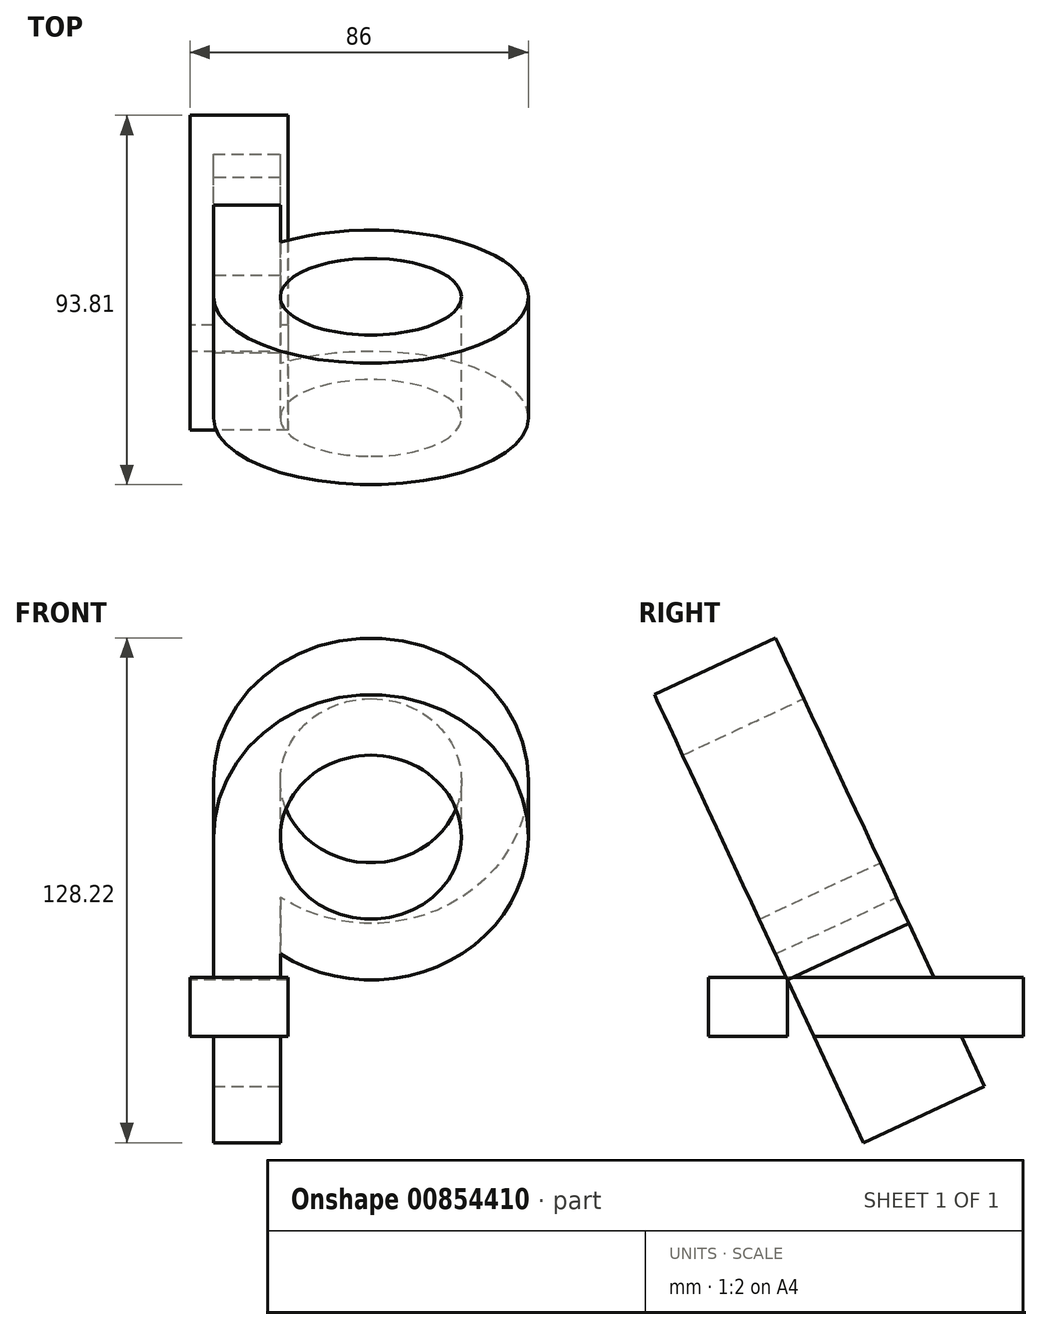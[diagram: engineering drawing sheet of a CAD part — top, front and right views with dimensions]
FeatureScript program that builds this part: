
annotation { "Feature Type Name" : "Feature", "Feature Type Description" : "" }
export const myFeature = defineFeature(function(context is Context, id is Id, definition is map)
    precondition{}
    {
        {
            var Q0;
            Q0=qCreatedBy(makeId("Top.planeOp"),FACE);
            var sketch = newSketch(context, id + "F0", { "sketchPlane" : qUnion([Q0])});
            skLineSegment(sketch, "E0", {"start": v(-43.75, 0) * mm, "end": v(54.87, 0) * mm});
            skSolve(sketch);
        }
        {
            var Q0;
            Q0=sQuery(id+"F0.wireOp",EDGE,"E0");
            cPlane(context, id + "F1", {"entities" : qUnion([Q0]), "cplaneType" : CPlaneType.LINE_ANGLE, "offset" : 25 * mm, "angle" : 25 * degree, "width" : 150 * mm, "height" : 150 * mm});
        }
        {
            var Q0;
            Q0=qCreatedBy(id+"F1.planeOp",FACE);
            var sketch = newSketch(context, id + "F2", { "sketchPlane" : qUnion([Q0])});
            skCircle(sketch, "E1", {"center": v(0, 0) * mm, "radius": 23 * mm});
            skCircle(sketch, "E2", {"center": v(0, 0) * mm, "radius": 40 * mm});
            skSolve(sketch);
        }
        {
            var Q0;
            Q0=qCreatedBy(makeId("Right.planeOp"),FACE);
            var sketch = newSketch(context, id + "F3", { "sketchPlane" : qUnion([Q0])});
            skLineSegment(sketch, "E3.0", {"start": v(-16.9, 36.25) * mm, "end": v(16.9, -36.25) * mm});
            skPoint(sketch, "E4.0", {"position": v(0, 0) * mm});
            skLineSegment(sketch, "E5", {"start": v(-36.47, -65) * mm, "end": v(44.94, -65) * mm});
            skSolve(sketch);
        }
        {
            var Q0;
            Q0=makeQuery(id+"F2.imprint","IMPRINT",FACE,{"disambiguationData":[TD([[makeQuery(id+"F2.imprint","IMPRINT",EDGE,{"derivedFrom":sQuery(id+"F2.wireOp",EDGE,"E1")}),-1.0]])]});
            extrude(context, id + "F4", {"entities" : qUnion([Q0]), "oppositeDirection" : true, "depth" : 34 * mm, "offsetDistance" : 25 * mm});
        }
        {
            var Q0;
            Q0=qCreatedBy(makeId("Right.planeOp"),FACE);
            var sketch = newSketch(context, id + "F5", { "sketchPlane" : qUnion([Q0])});
            skLineSegment(sketch, "E6.0", {"start": v(-47.72, 21.88) * mm, "end": v(-13.9, -50.62) * mm});
            skLineSegment(sketch, "E7", {"start": v(-13.9, -50.62) * mm, "end": v(-3.88, -72.13) * mm});
            skLineSegment(sketch, "E8.0", {"start": v(-16.9, 36.25) * mm, "end": v(16.9, -36.25) * mm});
            skLineSegment(sketch, "E9", {"start": v(16.9, -36.25) * mm, "end": v(33.41, -71.65) * mm});
            skLineSegment(sketch, "E10.0", {"start": v(-36.47, -50) * mm, "end": v(49.3, -50) * mm});
            skLineSegment(sketch, "E11", {"start": v(-13.9, -50.62) * mm, "end": v(-13.9, -68.72) * mm});
            skLineSegment(sketch, "E12.0", {"start": v(-36.47, -65) * mm, "end": v(44.94, -65) * mm});
            skLineSegment(sketch, "E13", {"start": v(-13.9, -65) * mm, "end": v(-33.9, -65) * mm});
            skLineSegment(sketch, "E14", {"start": v(-13.9, -65) * mm, "end": v(46.1, -65) * mm});
            skLineSegment(sketch, "E15", {"start": v(-33.9, -65) * mm, "end": v(-33.9, -50) * mm});
            skLineSegment(sketch, "E16", {"start": v(46.1, -65) * mm, "end": v(46.1, -50) * mm});
            skSolve(sketch);
        }
        {
            var Q0;
            Q0=qCreatedBy(makeId("Right.planeOp"),FACE);
            cPlane(context, id + "F6", {"entities" : qUnion([Q0]), "cplaneType" : CPlaneType.OFFSET, "offset" : 46 * mm, "oppositeDirection" : true, "width" : 150 * mm, "height" : 150 * mm});
        }
        {
            var Q0;
            Q0=qCreatedBy(id+"F6.planeOp",FACE);
            var sketch = newSketch(context, id + "F7", { "sketchPlane" : qUnion([Q0])});
            skLineSegment(sketch, "E17.0.0", {"start": v(-33.9, -50) * mm, "end": v(-33.9, -65) * mm});
            skLineSegment(sketch, "E17.0.1", {"start": v(-33.9, -65) * mm, "end": v(-13.9, -65) * mm});
            skLineSegment(sketch, "E17.0.2", {"start": v(-13.9, -65) * mm, "end": v(-13.9, -50.62) * mm});
            skLineSegment(sketch, "E17.0.3", {"start": v(-13.9, -50.62) * mm, "end": v(-14.2, -50) * mm});
            skLineSegment(sketch, "E17.0.4", {"start": v(-14.2, -50) * mm, "end": v(-33.9, -50) * mm});
            skLineSegment(sketch, "E18.0.0", {"start": v(-7.2, -65) * mm, "end": v(-13.9, -50.62) * mm});
            skLineSegment(sketch, "E18.0.1", {"start": v(-13.9, -50.62) * mm, "end": v(-13.9, -65) * mm});
            skLineSegment(sketch, "E18.0.2", {"start": v(-13.9, -65) * mm, "end": v(-7.2, -65) * mm});
            skLineSegment(sketch, "E19.0.0", {"start": v(23.32, -50) * mm, "end": v(-14.2, -50) * mm});
            skLineSegment(sketch, "E19.0.1", {"start": v(-14.2, -50) * mm, "end": v(-13.9, -50.62) * mm});
            skLineSegment(sketch, "E19.0.2", {"start": v(-13.9, -50.62) * mm, "end": v(-7.2, -65) * mm});
            skLineSegment(sketch, "E19.0.3", {"start": v(-7.2, -65) * mm, "end": v(30.3, -65) * mm});
            skLineSegment(sketch, "E19.0.4", {"start": v(30.3, -65) * mm, "end": v(23.32, -50) * mm});
            skLineSegment(sketch, "E20.0.0", {"start": v(46.1, -50) * mm, "end": v(23.32, -50) * mm});
            skLineSegment(sketch, "E20.0.1", {"start": v(23.32, -50) * mm, "end": v(30.3, -65) * mm});
            skLineSegment(sketch, "E20.0.2", {"start": v(30.3, -65) * mm, "end": v(46.1, -65) * mm});
            skLineSegment(sketch, "E20.0.3", {"start": v(46.1, -65) * mm, "end": v(46.1, -50) * mm});
            skSolve(sketch);
        }
        {
            var Q0;
            Q0=makeQuery(id+"F7.imprint","IMPRINT",FACE,{"disambiguationData":[TD([[makeQuery(id+"F7.imprint","IMPRINT",EDGE,{"derivedFrom":sQuery(id+"F7.wireOp",EDGE,"E17.0.0")}),1.0]])]});
            var Q1;
            Q1=makeQuery(id+"F7.imprint","IMPRINT",FACE,{"disambiguationData":[TD([[makeQuery(id+"F7.imprint","IMPRINT",EDGE,{"derivedFrom":sQuery(id+"F7.wireOp",EDGE,"E18.0.1")}),1.0]])]});
            var Q2;
            Q2=makeQuery(id+"F7.imprint","IMPRINT",FACE,{"disambiguationData":[TD([[makeQuery(id+"F7.imprint","IMPRINT",EDGE,{"derivedFrom":sQuery(id+"F7.wireOp",EDGE,"E19.0.0")}),1.0]])]});
            var Q3;
            Q3=makeQuery(id+"F7.imprint","IMPRINT",FACE,{"disambiguationData":[TD([[makeQuery(id+"F7.imprint","IMPRINT",EDGE,{"derivedFrom":sQuery(id+"F7.wireOp",EDGE,"E20.0.0")}),1.0]])]});
            extrude(context, id + "F8", {"entities" : qUnion([Q0, Q1, Q2, Q3]), "depth" : 25 * mm, "offsetDistance" : 25 * mm});
        }
        {
            var Q0;
            Q0=qCreatedBy(id+"F1.planeOp",FACE);
            var sketch = newSketch(context, id + "F9", { "sketchPlane" : qUnion([Q0])});
            skCircle(sketch, "E21.0", {"center": v(0, 0) * mm, "radius": 40 * mm});
            skLineSegment(sketch, "E22.0", {"start": v(43.75, 0) * mm, "end": v(-54.87, 0) * mm});
            skLineSegment(sketch, "E23", {"start": v(40, 0) * mm, "end": v(40, -93.36) * mm});
            skCircle(sketch, "E24.0", {"center": v(0, 0) * mm, "radius": 23 * mm});
            skLineSegment(sketch, "E25", {"start": v(23, 0) * mm, "end": v(23, -93.57) * mm});
            skLineSegment(sketch, "E26", {"start": v(40, -85.63) * mm, "end": v(23, -85.63) * mm});
            skSolve(sketch);
        }
        {
            var Q0;
            {var subQ5=sQuery(id+"F9.wireOp",EDGE,"E26");Q0=makeQuery(id+"F9.imprint","IMPRINT",FACE,{"disambiguationData":[TD([[makeQuery(id+"F9.imprint","IMPRINT",EDGE,{"derivedFrom":subQ5}),-1.0]])]});}
            var Q1;
            Q1=makeQuery(id+"F4.opExtrude","CAP_FACE",FACE,{"disambiguationData":[OSD([sQuery(id+"F2.wireOp",EDGE,"E1"),sQuery(id+"F2.wireOp",EDGE,"E2")])],"isStart":false});
            extrude(context, id + "F10", {"entities" : qUnion([Q0]), "operationType" : NewBodyOperationType.ADD, "endBound" : BoundingType.UP_TO_SURFACE, "oppositeDirection" : true, "depth" : 25 * mm, "endBoundEntityFace" : qUnion([Q1]), "offsetDistance" : 25 * mm});
        }
    });
